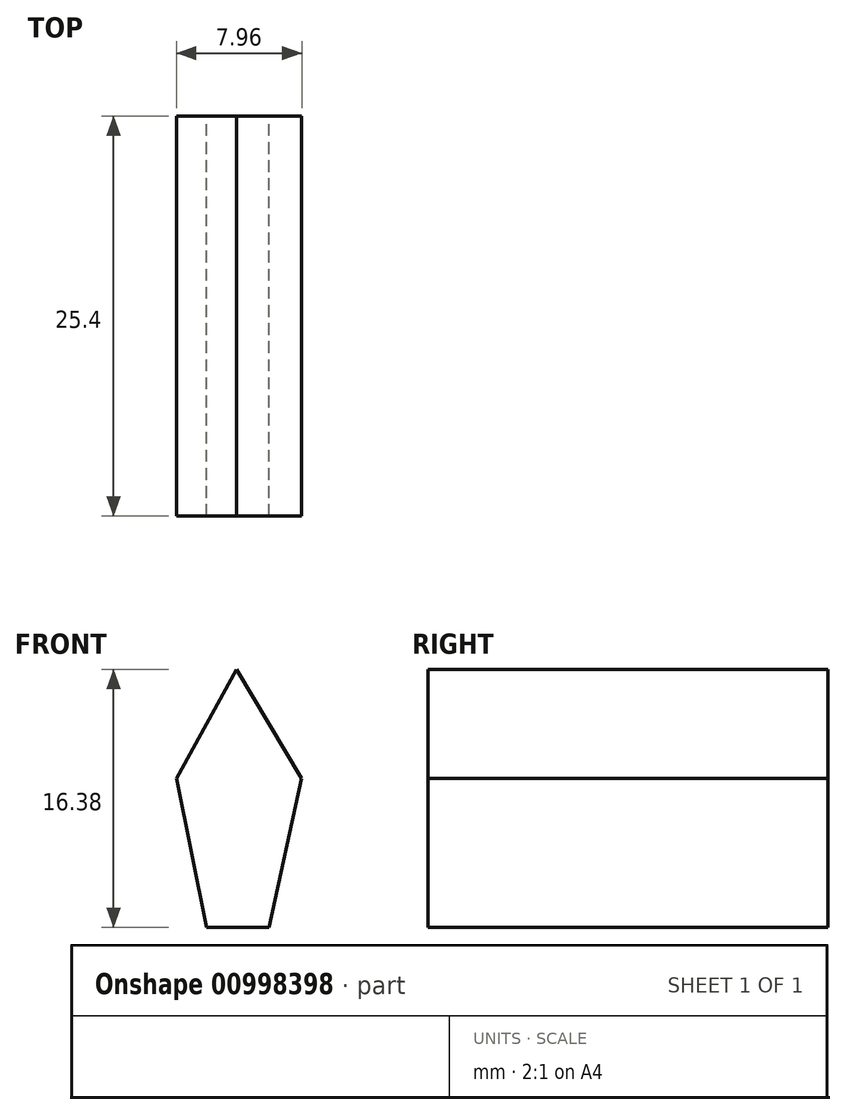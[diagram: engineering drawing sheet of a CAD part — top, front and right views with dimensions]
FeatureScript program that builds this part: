
annotation { "Feature Type Name" : "Feature", "Feature Type Description" : "" }
export const myFeature = defineFeature(function(context is Context, id is Id, definition is map)
    precondition{}
    {
        {
            var Q0;
            Q0=qCreatedBy(makeId("Front.planeOp"),FACE);
            var sketch = newSketch(context, id + "F0", { "sketchPlane" : qUnion([Q0])});
            skLineSegment(sketch, "E0", {"start": v(-3.82, 0) * mm, "end": v(4.14, 0) * mm});
            skLineSegment(sketch, "E1", {"start": v(4.14, 0) * mm, "end": v(0, 6.92) * mm});
            skLineSegment(sketch, "E2", {"start": v(0, 6.92) * mm, "end": v(-3.82, 0) * mm});
            skLineSegment(sketch, "E3", {"start": v(-3.82, 0) * mm, "end": v(-1.9, -9.46) * mm});
            skPoint(sketch, "E3.endSnap0", {"position": v(-1.9, 3.46) * mm});
            skLineSegment(sketch, "E4", {"start": v(-1.9, -9.46) * mm, "end": v(2.07, -9.46) * mm});
            skLineSegment(sketch, "E5", {"start": v(2.07, -9.46) * mm, "end": v(4.14, 0) * mm});
            skSolve(sketch);
        }
        {
            var Q0;
            Q0=makeQuery(id+"F0.imprint","IMPRINT",FACE,{"disambiguationData":[TD([[makeQuery(id+"F0.imprint","IMPRINT",EDGE,{"derivedFrom":sQuery(id+"F0.wireOp",EDGE,"E0")}),-1.0]])]});
            var Q1;
            Q1=makeQuery(id+"F0.imprint","IMPRINT",FACE,{"disambiguationData":[TD([[makeQuery(id+"F0.imprint","IMPRINT",EDGE,{"derivedFrom":sQuery(id+"F0.wireOp",EDGE,"E0")}),1.0]])]});
            extrude(context, id + "F1", {"entities" : qUnion([Q0, Q1]), "depth" : 25.4 * mm, "offsetDistance" : 25.4 * mm});
        }
    });
